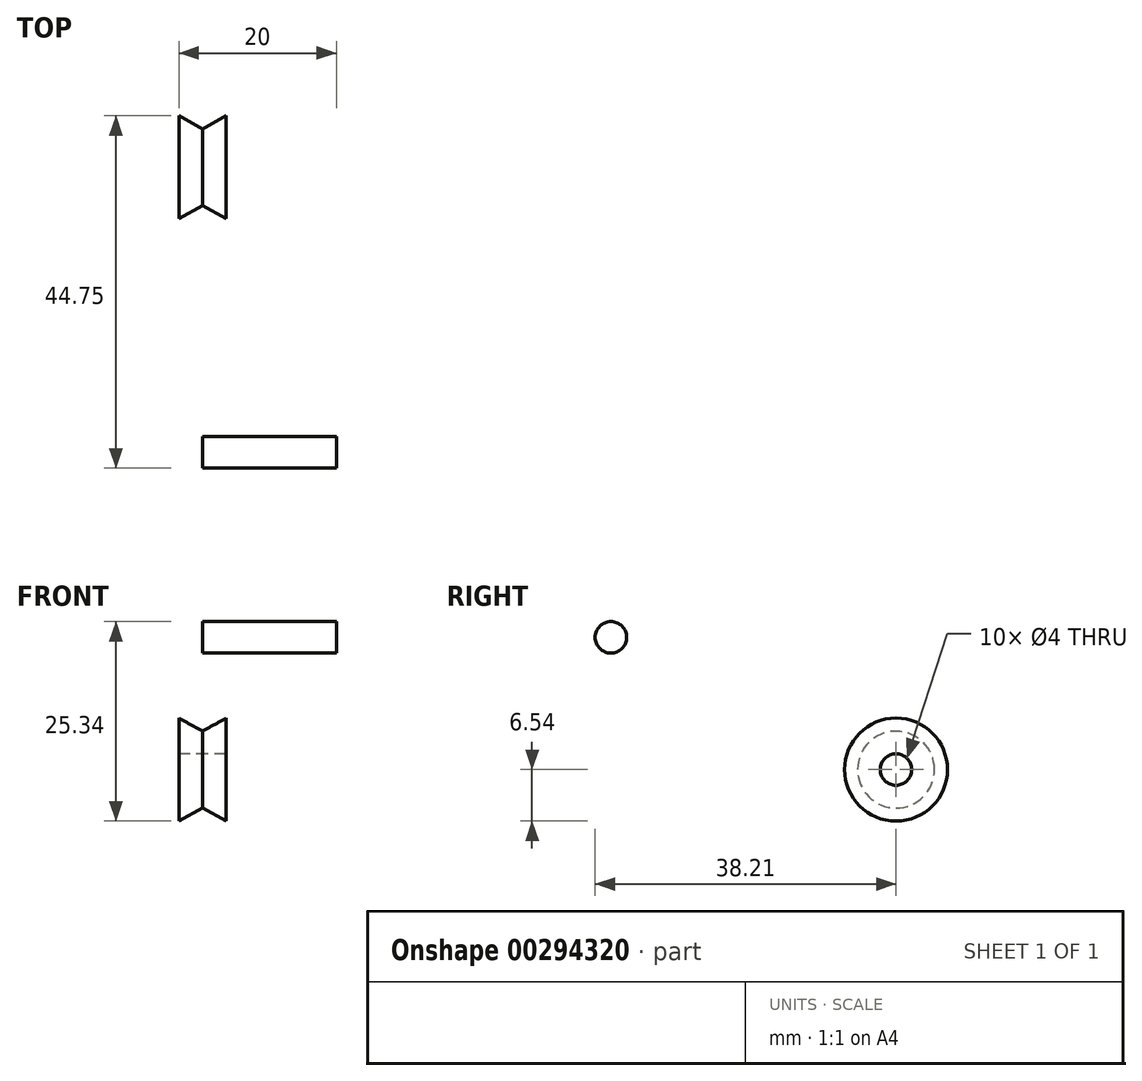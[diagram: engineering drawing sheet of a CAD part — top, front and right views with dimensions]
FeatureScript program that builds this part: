
annotation { "Feature Type Name" : "Feature", "Feature Type Description" : "" }
export const myFeature = defineFeature(function(context is Context, id is Id, definition is map)
    precondition{}
    {
        {
            var Q0;
            Q0=qCreatedBy(makeId("Front.planeOp"),FACE);
            var sketch = newSketch(context, id + "F0", { "sketchPlane" : qUnion([Q0])});
            skLineSegment(sketch, "E0", {"start": v(0, 2) * mm, "end": v(3, 2) * mm});
            skLineSegment(sketch, "E1", {"start": v(3, 2) * mm, "end": v(3, 6.54) * mm});
            skLineSegment(sketch, "E2", {"start": v(3, 6.54) * mm, "end": v(0, 4.88) * mm});
            skLineSegment(sketch, "E3.MirrorCS", {"start": v(-3, 6.54) * mm, "end": v(0, 4.88) * mm});
            skLineSegment(sketch, "E4.MirrorCS", {"start": v(-3, 2) * mm, "end": v(-3, 6.54) * mm});
            skLineSegment(sketch, "E5.MirrorCS", {"start": v(0, 2) * mm, "end": v(-3, 2) * mm});
            skLineSegment(sketch, "E6", {"start": v(-11.5, 0) * mm, "end": v(14.25, 0) * mm, "construction": true});
            skSolve(sketch);
        }
        {
            var Q0;
            Q0 = qSketchRegion(id + "F0", true);
            var Q1;
            Q1=sQuery(id+"F0.wireOp",EDGE,"E6");
            revolve(context, id + "F1", {"entities" : qUnion([Q0]), "axis" : qUnion([Q1]), "revolveType" : RevolveType.FULL});
        }
        {
            var Q0;
            Q0=qCreatedBy(makeId("Right.planeOp"),FACE);
            var sketch = newSketch(context, id + "F2", { "sketchPlane" : qUnion([Q0])});
            skCircle(sketch, "E7", {"center": v(-36.21, 16.8) * mm, "radius": 2 * mm});
            skSolve(sketch);
        }
        {
            var Q0;
            Q0 = qSketchRegion(id + "F2", true);
            extrude(context, id + "F3", {"entities" : qUnion([Q0]), "depth" : 17 * mm});
        }
    });
